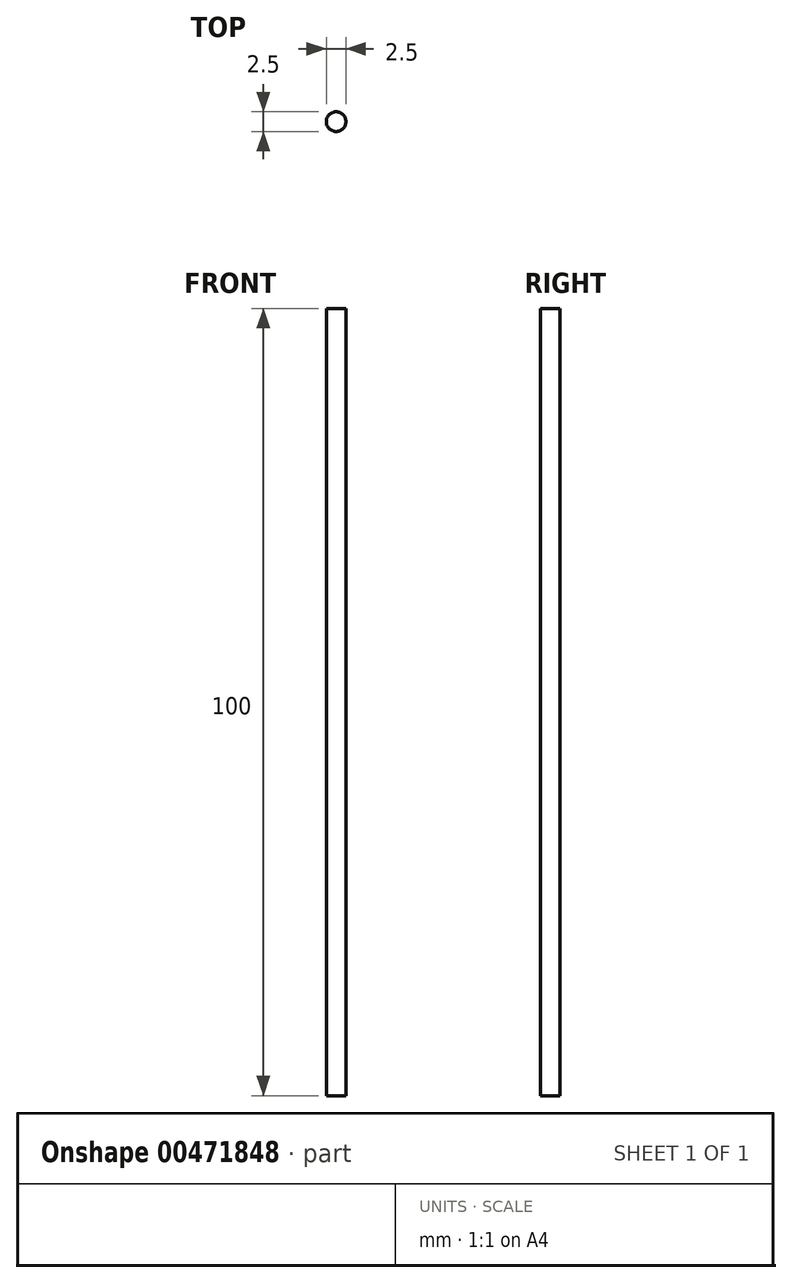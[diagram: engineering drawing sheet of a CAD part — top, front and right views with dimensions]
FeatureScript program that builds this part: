
annotation { "Feature Type Name" : "Feature", "Feature Type Description" : "" }
export const myFeature = defineFeature(function(context is Context, id is Id, definition is map)
    precondition{}
    {
        {
            var Q0;
            Q0=qCreatedBy(makeId("Top.planeOp"),FACE);
            var sketch = newSketch(context, id + "F0", { "sketchPlane" : qUnion([Q0])});
            skCircle(sketch, "E0", {"center": v(0, 0) * mm, "radius": 1.25 * mm});
            skSolve(sketch);
        }
        {
            var Q0;
            Q0 = qSketchRegion(id + "F0", true);
            var Q1;
            Q1=makeQuery(id+"F0.imprint","IMPRINT",FACE,{"disambiguationData":[TD([[makeQuery(id+"F0.imprint","IMPRINT",EDGE,{"derivedFrom":sQuery(id+"F0.wireOp",EDGE,"E0")}),1.0]])]});
            extrude(context, id + "F1", {"entities" : qUnion([Q0, Q1]), "depth" : 100 * mm});
        }
    });
